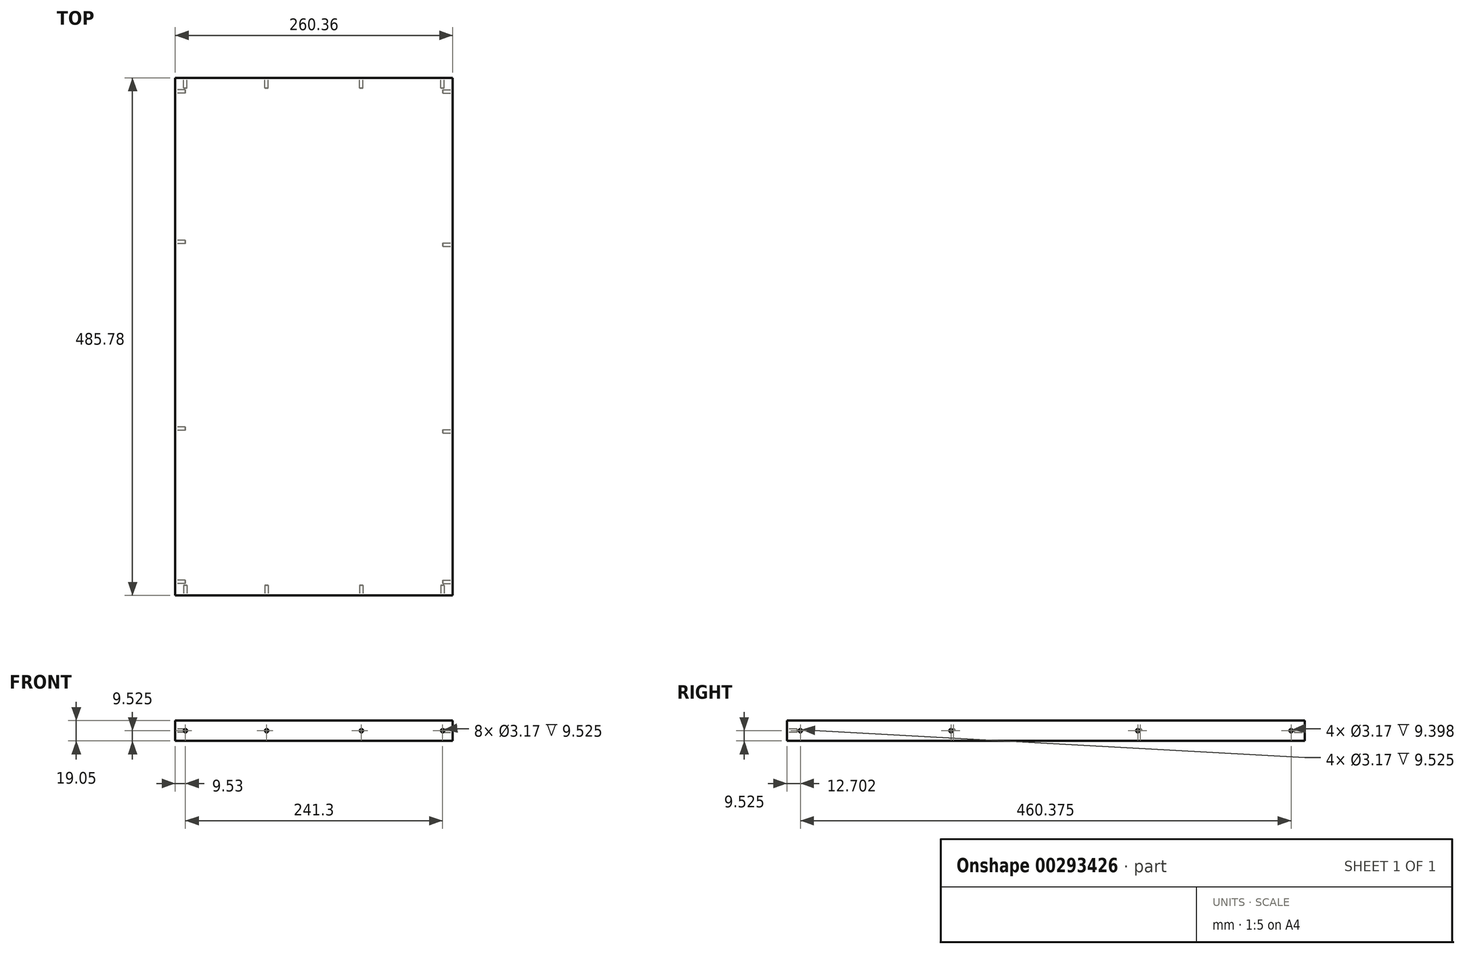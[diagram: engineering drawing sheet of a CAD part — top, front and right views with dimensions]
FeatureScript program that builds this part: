
annotation { "Feature Type Name" : "Feature", "Feature Type Description" : "" }
export const myFeature = defineFeature(function(context is Context, id is Id, definition is map)
    precondition{}
    {
        {
            var Q0;
            Q0=qCreatedBy(makeId("Top.planeOp"),FACE);
            var sketch = newSketch(context, id + "F0", { "sketchPlane" : qUnion([Q0])});
            skLineSegment(sketch, "E0.bottom", {"start": v(130.18, -242.89) * mm, "end": v(-130.17, -242.89) * mm});
            skLineSegment(sketch, "E0.top", {"start": v(130.18, 242.89) * mm, "end": v(-130.17, 242.89) * mm});
            skLineSegment(sketch, "E0.left", {"start": v(130.18, -242.89) * mm, "end": v(130.18, 242.89) * mm});
            skLineSegment(sketch, "E0.right", {"start": v(-130.18, -242.89) * mm, "end": v(-130.17, 242.89) * mm});
            skPoint(sketch, "E0.middle", {"position": v(0, 0) * mm});
            skSolve(sketch);
        }
        {
            var Q0;
            Q0=makeQuery(id+"F0.imprint","IMPRINT",FACE,{"disambiguationData":[TD([[makeQuery(id+"F0.imprint","IMPRINT",EDGE,{"derivedFrom":sQuery(id+"F0.wireOp",EDGE,"E0.bottom")}),-1.0]])]});
            extrude(context, id + "F1", {"entities" : qUnion([Q0]), "depth" : 19.05 * mm});
        }
        {
            var Q0;
            Q0=makeQuery(id+"F1.opExtrude","SWEPT_FACE",FACE,{"disambiguationData":[OSD([sQuery(id+"F0.wireOp",EDGE,"E0.left")])]});
            var sketch = newSketch(context, id + "F2", { "sketchPlane" : qUnion([Q0])});
            skCircle(sketch, "E1", {"center": v(-230.19, 9.53) * mm, "radius": 1.59 * mm});
            skCircle(sketch, "E2", {"center": v(230.19, 9.53) * mm, "radius": 1.59 * mm});
            skCircle(sketch, "E3", {"center": v(-88.9, 9.53) * mm, "radius": 1.59 * mm});
            skCircle(sketch, "E4", {"center": v(86.36, 9.53) * mm, "radius": 1.59 * mm});
            skSolve(sketch);
        }
        {
            var Q0;
            Q0=makeQuery(id+"F1.opExtrude","SWEPT_FACE",FACE,{"disambiguationData":[OSD([sQuery(id+"F0.wireOp",EDGE,"E0.right")])]});
            var sketch = newSketch(context, id + "F3", { "sketchPlane" : qUnion([Q0])});
            skCircle(sketch, "E5", {"center": v(-230.19, 9.53) * mm, "radius": 1.59 * mm});
            skCircle(sketch, "E6", {"center": v(230.19, 9.53) * mm, "radius": 1.59 * mm});
            skCircle(sketch, "E7", {"center": v(-88.9, 9.53) * mm, "radius": 1.59 * mm});
            skCircle(sketch, "E8", {"center": v(86.36, 9.53) * mm, "radius": 1.59 * mm});
            skSolve(sketch);
        }
        {
            var Q0;
            Q0=makeQuery(id+"F2.imprint","IMPRINT",FACE,{"disambiguationData":[TD([[makeQuery(id+"F2.imprint","IMPRINT",EDGE,{"derivedFrom":sQuery(id+"F2.wireOp",EDGE,"E2")}),1.0]])]});
            var Q1;
            Q1=makeQuery(id+"F2.imprint","IMPRINT",FACE,{"disambiguationData":[TD([[makeQuery(id+"F2.imprint","IMPRINT",EDGE,{"derivedFrom":sQuery(id+"F2.wireOp",EDGE,"E4")}),1.0]])]});
            var Q2;
            Q2=makeQuery(id+"F2.imprint","IMPRINT",FACE,{"disambiguationData":[TD([[makeQuery(id+"F2.imprint","IMPRINT",EDGE,{"derivedFrom":sQuery(id+"F2.wireOp",EDGE,"E3")}),1.0]])]});
            var Q3;
            Q3=makeQuery(id+"F2.imprint","IMPRINT",FACE,{"disambiguationData":[TD([[makeQuery(id+"F2.imprint","IMPRINT",EDGE,{"derivedFrom":sQuery(id+"F2.wireOp",EDGE,"E1")}),1.0]])]});
            extrude(context, id + "F4", {"entities" : qUnion([Q0, Q1, Q2, Q3]), "operationType" : NewBodyOperationType.REMOVE, "oppositeDirection" : true, "depth" : 9.4 * mm});
        }
        {
            var Q0;
            Q0=makeQuery(id+"F3.imprint","IMPRINT",FACE,{"disambiguationData":[TD([[makeQuery(id+"F3.imprint","IMPRINT",EDGE,{"derivedFrom":sQuery(id+"F3.wireOp",EDGE,"E5")}),1.0]])]});
            var Q1;
            Q1=makeQuery(id+"F3.imprint","IMPRINT",FACE,{"disambiguationData":[TD([[makeQuery(id+"F3.imprint","IMPRINT",EDGE,{"derivedFrom":sQuery(id+"F3.wireOp",EDGE,"E7")}),1.0]])]});
            var Q2;
            Q2=makeQuery(id+"F3.imprint","IMPRINT",FACE,{"disambiguationData":[TD([[makeQuery(id+"F3.imprint","IMPRINT",EDGE,{"derivedFrom":sQuery(id+"F3.wireOp",EDGE,"E8")}),1.0]])]});
            var Q3;
            Q3=makeQuery(id+"F3.imprint","IMPRINT",FACE,{"disambiguationData":[TD([[makeQuery(id+"F3.imprint","IMPRINT",EDGE,{"derivedFrom":sQuery(id+"F3.wireOp",EDGE,"E6")}),1.0]])]});
            extrude(context, id + "F5", {"entities" : qUnion([Q0, Q1, Q2, Q3]), "operationType" : NewBodyOperationType.REMOVE, "oppositeDirection" : true, "depth" : 9.52 * mm});
        }
        {
            var Q0;
            Q0=makeQuery(id+"F1.opExtrude","SWEPT_FACE",FACE,{"disambiguationData":[OSD([sQuery(id+"F0.wireOp",EDGE,"E0.bottom")])]});
            var sketch = newSketch(context, id + "F6", { "sketchPlane" : qUnion([Q0])});
            skCircle(sketch, "E9", {"center": v(-120.65, 9.53) * mm, "radius": 1.59 * mm});
            skCircle(sketch, "E10", {"center": v(-44.45, 9.53) * mm, "radius": 1.59 * mm});
            skCircle(sketch, "E11", {"center": v(44.45, 9.53) * mm, "radius": 1.59 * mm});
            skCircle(sketch, "E12", {"center": v(120.65, 9.53) * mm, "radius": 1.59 * mm});
            skSolve(sketch);
        }
        {
            var Q0;
            Q0=makeQuery(id+"F1.opExtrude","SWEPT_FACE",FACE,{"disambiguationData":[OSD([sQuery(id+"F0.wireOp",EDGE,"E0.top")])]});
            var sketch = newSketch(context, id + "F7", { "sketchPlane" : qUnion([Q0])});
            skCircle(sketch, "E13", {"center": v(-120.65, 9.53) * mm, "radius": 1.59 * mm});
            skCircle(sketch, "E14", {"center": v(-44.45, 9.53) * mm, "radius": 1.59 * mm});
            skCircle(sketch, "E15", {"center": v(44.45, 9.53) * mm, "radius": 1.59 * mm});
            skCircle(sketch, "E16", {"center": v(120.65, 9.53) * mm, "radius": 1.59 * mm});
            skSolve(sketch);
        }
        {
            var Q0;
            Q0=makeQuery(id+"F7.imprint","IMPRINT",FACE,{"disambiguationData":[TD([[makeQuery(id+"F7.imprint","IMPRINT",EDGE,{"derivedFrom":sQuery(id+"F7.wireOp",EDGE,"E13")}),1.0]])]});
            var Q1;
            Q1=makeQuery(id+"F7.imprint","IMPRINT",FACE,{"disambiguationData":[TD([[makeQuery(id+"F7.imprint","IMPRINT",EDGE,{"derivedFrom":sQuery(id+"F7.wireOp",EDGE,"E14")}),1.0]])]});
            var Q2;
            Q2=makeQuery(id+"F7.imprint","IMPRINT",FACE,{"disambiguationData":[TD([[makeQuery(id+"F7.imprint","IMPRINT",EDGE,{"derivedFrom":sQuery(id+"F7.wireOp",EDGE,"E15")}),1.0]])]});
            var Q3;
            Q3=makeQuery(id+"F7.imprint","IMPRINT",FACE,{"disambiguationData":[TD([[makeQuery(id+"F7.imprint","IMPRINT",EDGE,{"derivedFrom":sQuery(id+"F7.wireOp",EDGE,"E16")}),1.0]])]});
            extrude(context, id + "F8", {"entities" : qUnion([Q0, Q1, Q2, Q3]), "operationType" : NewBodyOperationType.REMOVE, "oppositeDirection" : true, "depth" : 9.52 * mm});
        }
        {
            var Q0;
            Q0=makeQuery(id+"F6.imprint","IMPRINT",FACE,{"disambiguationData":[TD([[makeQuery(id+"F6.imprint","IMPRINT",EDGE,{"derivedFrom":sQuery(id+"F6.wireOp",EDGE,"E12")}),1.0]])]});
            var Q1;
            Q1=makeQuery(id+"F6.imprint","IMPRINT",FACE,{"disambiguationData":[TD([[makeQuery(id+"F6.imprint","IMPRINT",EDGE,{"derivedFrom":sQuery(id+"F6.wireOp",EDGE,"E11")}),1.0]])]});
            var Q2;
            Q2=makeQuery(id+"F6.imprint","IMPRINT",FACE,{"disambiguationData":[TD([[makeQuery(id+"F6.imprint","IMPRINT",EDGE,{"derivedFrom":sQuery(id+"F6.wireOp",EDGE,"E10")}),1.0]])]});
            var Q3;
            Q3=makeQuery(id+"F6.imprint","IMPRINT",FACE,{"disambiguationData":[TD([[makeQuery(id+"F6.imprint","IMPRINT",EDGE,{"derivedFrom":sQuery(id+"F6.wireOp",EDGE,"E9")}),1.0]])]});
            extrude(context, id + "F9", {"entities" : qUnion([Q0, Q1, Q2, Q3]), "operationType" : NewBodyOperationType.REMOVE, "oppositeDirection" : true, "depth" : 9.52 * mm});
        }
    });
